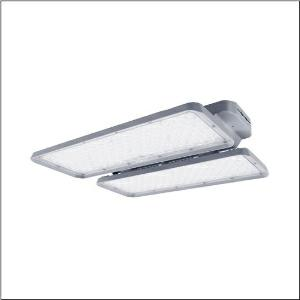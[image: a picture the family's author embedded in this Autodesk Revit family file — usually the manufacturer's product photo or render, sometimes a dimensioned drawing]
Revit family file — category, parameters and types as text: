
# Revit family: highbay_21-l_51hk41db4qca
name_source: partatom
category: Lighting Fixtures
units: mm (PartAtom-declared; Revit-internal decimal feet)

## family parameters
Cut with Voids When Loaded = No
Host = Face
Light Source = No
Part Type = Normal
Room Calculation Point = No
Round Connector Dimension = Use Diameter
Shared = No

## types (1)
- Highbay 21-L (1 x LED, 35600 lm, 200 W, 4000K)
    Apparent Load = 200 VA
    CIE Flux Codes = 87 97 99 100 100
    Color Rendering = 80
    Color Temperature = 4000K
    Default Elevation = 1800 mm
    Description = Highbay 21-L, LED high bay luminaire, primary light control with lens, of PC, light emission: direct distribution, primary light characteristic: symmetric, installation type: suspended mounting, surface-mounted, LED, rated luminous flux: 35.600lm, luminous efficacy: 178lm/W, light colour: 840, colour temperature: 4000K, with terminal, 5-pole, max. 2.5mm², mains connection: 220..240V, AC, 50Hz, rated input power: 200W, housing, of diecast aluminium, coated, grey, length: 471mm, width: 390mm, height: 87mm, protection rating (complete): IP66, insulation class (complete): insulation class I (protective earthing), certification: CE, ENEC, UKCA, protection symbol: D, impact resistance: IK08, permissible operating ambient temperature: -30..+60°C, corresponds to IFS (International Featured Standards) requirements for safety and quality in the food industry, LABS conformity tested according to VDMA 24364:2018-05, packaging unit: 1 piece
    Height = 89 mm
    Lamp = 1 x LED
    Lamp Light Flux = 35600 lm
    Lamp Power = 200 W
    Lamp count = 1
    Length = 471 mm
    Luminous efficacy = 178 lm/W
    Manufacturer = Siteco
    ModVariant = No
    Model = 51HK41DB4QCA
    Mounting Place = Ceiling
    Mounting Type = Pendant
    Number of Poles = 1
    OnlyDefault = Yes
    Power Factor = 1
    Product Name = Highbay 21-L
    Product group = LED high bay luminaire
    ProductGroupID = 903
    Protection Class = Protection class I
    Protection Degree = IP 66
    RLX_Detail_Level = 1
    RLX_Emergency_Light_Flux = 0 lm
    RLX_Emergency_Type = 0
    RLX_Emergency_Type_DB = No
    RlxData = <blob elided: 25429 chars, md5=b94f9121>
    Socket = socket
    Standby Power = 0 W
    System Light Flux = 35600 lm
    System Power = 200 W
    Type Comments = Product without accessories
    Type Image = l_1276530.jpg
    URL = http://relux.com
    VarID = ---
    Voltage = 0 V
    Weight = 0.00 kg
    Width = 390 mm

## geometry (parser evidence)
native form markers: Blend x4, Sweep x11
no freeform markers — native parametric forms only
